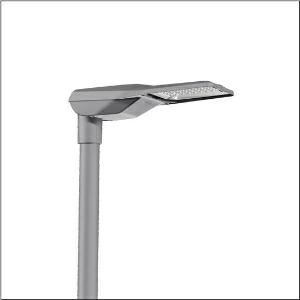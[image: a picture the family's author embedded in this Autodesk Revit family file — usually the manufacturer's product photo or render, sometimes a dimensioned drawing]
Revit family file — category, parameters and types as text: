
# Revit family: streetlight_sl_21_iq_mini___st0_8a_5xe2c21g08hb_0b1a
name_source: partatom
category: Lighting Fixtures
units: mm (PartAtom-declared; Revit-internal decimal feet)

## family parameters
Cut with Voids When Loaded = No
Host = Face
Light Source = No
Part Type = Normal
Room Calculation Point = No
Round Connector Dimension = Use Diameter
Shared = No

## types (1)
- --- (1 x LED, 7830 lm, 70.9 W, 2200K)
    Apparent Load = 71 VA
    CIE Flux Codes = 38 75 97 100 100
    Color Rendering = 70
    Color Temperature = 2200K
    Default Elevation = 1800 mm
    Description = Streetlight SL 21 iQ mini, mast luminaire, primary light control with lens, of PMMA, primary optical cover: cover, of toughened safety glass, transparent, light distribution: ST0.8a, light emission: direct distribution, primary light characteristic: asymmetric, installation type: post-top, side-entry, LED, High Power LED, rated luminous flux: 7.830lm, luminous efficacy: 110lm/W, light colour: 722, colour temperature: 2200K, control: Street-Remote, Auto-Match, Temp-Guard, Lumen-Switch, Night-Set, Smart-Wire, Light-Fading, Desk-Remote (wireless, voltage-free reading and setting of iQ features in the workshop via application-optimized NFC function/RFID function), optimised constant luminous flux control (CLO 2.0), presetting dimming linear, mains connection: 220..240V, AC, 50/60Hz, start of lifetime: 71W, end of service life: 75W, reduction: 31W, luminaire housing, of diecast aluminium, powder-coated, Siteco® metallic grey (DB 702S), corrosivity category C5 mid according to DIN EN ISO 12944, please order mast flange separately, inclination adjustable: 0°, 5°, 10°, 15°, sealing non-destructively replaceable, multi-level sealing system, length: 628mm, width: 235mm, height: 110mm, mast flange for spigot size: 42mm (side-entry): 5XC10008XM4, 60/48mm (side-entry/post-top): 5XC10108XM2, 76/60mm (side-entry/post-top): 5XC10108XM1, protection rating (complete): IP66, insulation class (complete): insulation class II (safety insulation), certification: CE, ENEC, ENEC+, VDE, impact resistance: IK09, permissible operating ambient temperature for outdoor applications: -40..+50°C, standard-compliant lighting for roads and squares, packaging unit: 1 piece

Light Distribution: ST0.8a
    Height = 110 mm
    Lamp = 1 x LED
    Lamp Light Flux = 7830 lm
    Lamp Power = 70.9 W
    Lamp count = 1
    Length = 625 mm
    Luminous efficacy = 110 lm/W
    Manufacturer = Siteco
    ModVariant = No
    Model = 5XE2C21G08HB
    Number of Poles = 1
    OnlyDefault = Yes
    Power Factor = 1
    Product Name = Streetlight SL 21 iQ mini | ST0.8a
    Product group = mast luminaire | pylon top
    ProductGroupID = 6100
    Protection Class = Protection class II
    Protection Degree = IP 66
    RLX_Detail_Level = 1
    RLX_Emergency_Light_Flux = 0 lm
    RLX_Emergency_Type = 0
    RLX_Emergency_Type_DB = No
    RlxData = <blob elided: 92341 chars, md5=4ae03b1d>
    Socket = socket
    Standby Power = 0 W
    System Light Flux = 7830 lm
    System Power = 71 W
    Type Comments = factory setting: luminous flux: 100 % | dim-lin: 254 | 711 mA
    Type Image = l_1003519.jpg
    URL = http://relux.com
    VarID = @adj_107701
    Voltage = 0 V
    Weight = 0.00 kg
    Width = 234 mm

## geometry (parser evidence)
native form markers: Blend x4, Sweep x10
no freeform markers — native parametric forms only
